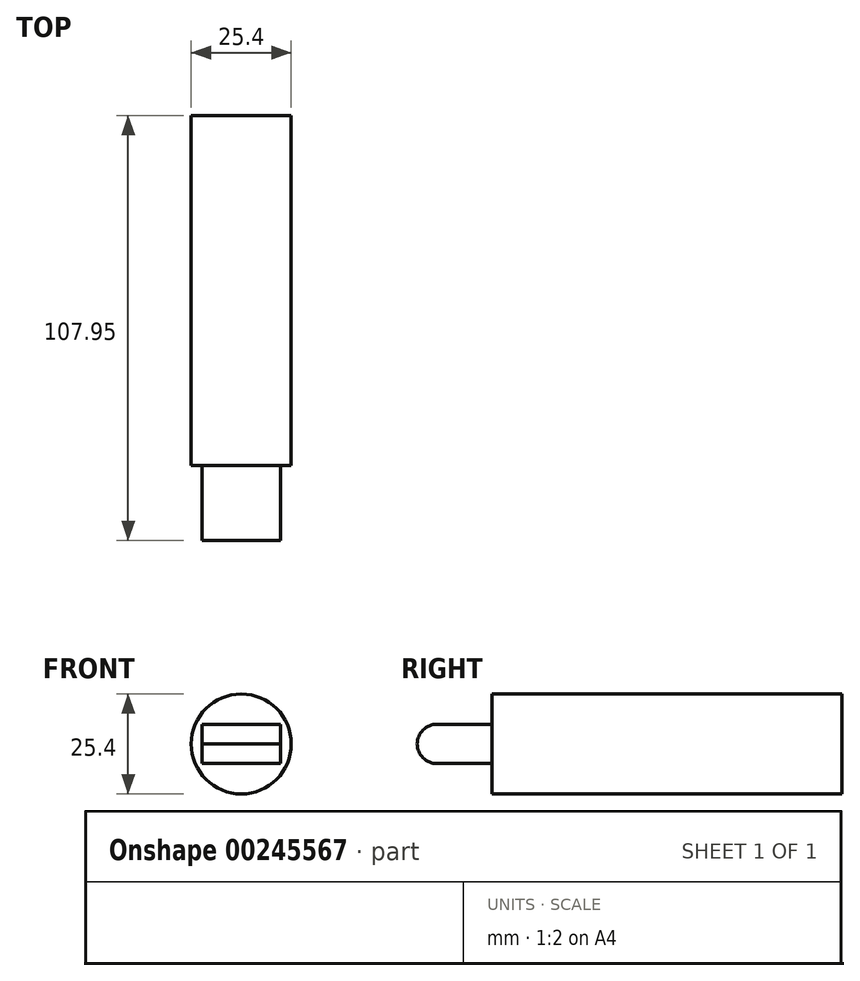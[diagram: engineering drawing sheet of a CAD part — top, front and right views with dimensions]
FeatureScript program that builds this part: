
annotation { "Feature Type Name" : "Feature", "Feature Type Description" : "" }
export const myFeature = defineFeature(function(context is Context, id is Id, definition is map)
    precondition{}
    {
        {
            var Q0;
            Q0=qCreatedBy(makeId("Front.planeOp"),FACE);
            var sketch = newSketch(context, id + "F0", { "sketchPlane" : qUnion([Q0])});
            skCircle(sketch, "E0", {"center": v(0, 0) * mm, "radius": 12.7 * mm});
            skSolve(sketch);
        }
        {
            var Q0;
            Q0=makeQuery(id+"F0.imprint","IMPRINT",FACE,{"disambiguationData":[TD([[makeQuery(id+"F0.imprint","IMPRINT",EDGE,{"derivedFrom":sQuery(id+"F0.wireOp",EDGE,"E0")}),1.0]])]});
            extrude(context, id + "F1", {"entities" : qUnion([Q0]), "depth" : 88.9 * mm});
        }
        {
            var Q0;
            Q0=makeQuery(id+"F1.opExtrude","CAP_FACE",FACE,{"disambiguationData":[OSD([sQuery(id+"F0.wireOp",EDGE,"E0")])],"isStart":false});
            var sketch = newSketch(context, id + "F2", { "sketchPlane" : qUnion([Q0])});
            skLineSegment(sketch, "E1.bottom", {"start": v(10, 5) * mm, "end": v(-10, 5) * mm});
            skLineSegment(sketch, "E1.top", {"start": v(10, -5) * mm, "end": v(-10, -5) * mm});
            skLineSegment(sketch, "E1.left", {"start": v(10, 5) * mm, "end": v(10, -5) * mm});
            skLineSegment(sketch, "E1.right", {"start": v(-10, 5) * mm, "end": v(-10, -5) * mm});
            skPoint(sketch, "E1.middle", {"position": v(0, 0) * mm});
            skSolve(sketch);
        }
        {
            var Q0;
            Q0=makeQuery(id+"F2.imprint","IMPRINT",FACE,{"disambiguationData":[TD([[makeQuery(id+"F2.imprint","IMPRINT",EDGE,{"derivedFrom":sQuery(id+"F2.wireOp",EDGE,"E1.bottom")}),1.0]])]});
            extrude(context, id + "F3", {"entities" : qUnion([Q0]), "operationType" : NewBodyOperationType.ADD, "depth" : 19.05 * mm});
        }
        {
            var Q0;
            Q0=makeQuery(id+"F3.opExtrude","CAP_EDGE",EDGE,{"disambiguationData":[OSD([sQuery(id+"F2.wireOp",EDGE,"E1.bottom")])],"isStart":false});
            var Q1;
            Q1=makeQuery(id+"F3.opExtrude","CAP_EDGE",EDGE,{"disambiguationData":[OSD([sQuery(id+"F2.wireOp",EDGE,"E1.top")])],"isStart":false});
            fillet(context, id + "F4", {"entities" : qUnion([Q0, Q1]), "radius" : 5.08 * mm, "tangentPropagation" : true, "allowEdgeOverflow" : false});
        }
    });
